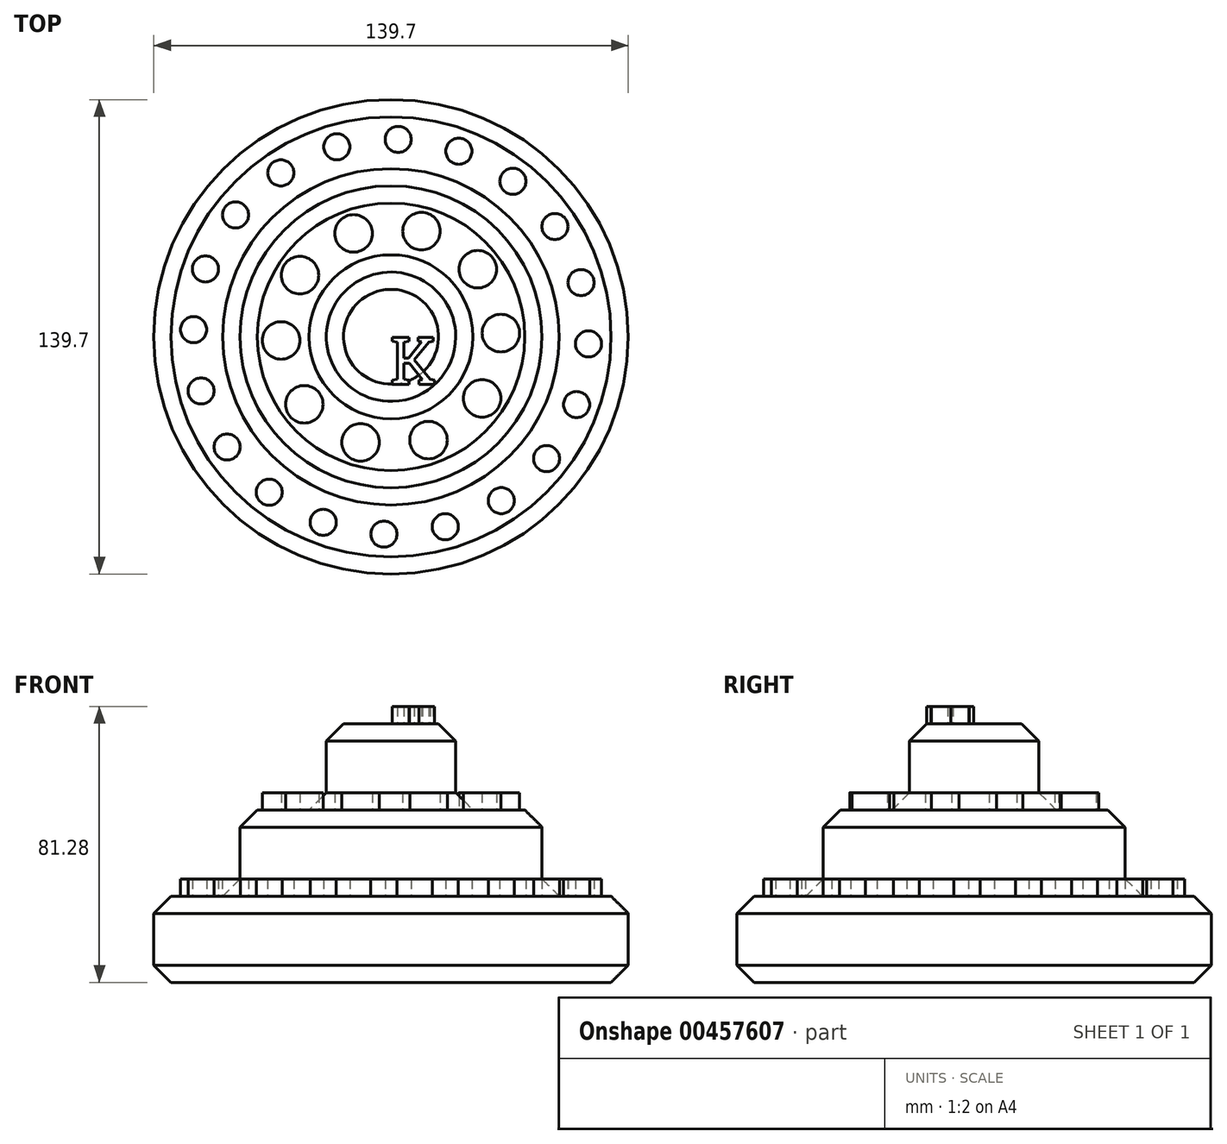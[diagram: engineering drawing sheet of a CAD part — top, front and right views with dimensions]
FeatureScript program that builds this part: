
annotation { "Feature Type Name" : "Feature", "Feature Type Description" : "" }
export const myFeature = defineFeature(function(context is Context, id is Id, definition is map)
    precondition{}
    {
        {
            var Q0;
            Q0=qCreatedBy(makeId("Top.planeOp"),FACE);
            var sketch = newSketch(context, id + "F0", { "sketchPlane" : qUnion([Q0])});
            skCircle(sketch, "E0", {"center": v(0, 0) * mm, "radius": 69.85 * mm});
            skSolve(sketch);
        }
        {
            var Q0;
            Q0=makeQuery(id+"F0.imprint","IMPRINT",FACE,{"disambiguationData":[TD([[makeQuery(id+"F0.imprint","IMPRINT",EDGE,{"derivedFrom":sQuery(id+"F0.wireOp",EDGE,"E0")}),1.0]])]});
            extrude(context, id + "F1", {"entities" : qUnion([Q0]), "depth" : 25.4 * mm});
        }
        {
            var Q0;
            Q0=qCreatedBy(makeId("Top.planeOp"),FACE);
            var sketch = newSketch(context, id + "F2", { "sketchPlane" : qUnion([Q0])});
            skCircle(sketch, "E1", {"center": v(0, 0) * mm, "radius": 44.45 * mm});
            skSolve(sketch);
        }
        {
            var Q0;
            Q0=makeQuery(id+"F2.imprint","IMPRINT",FACE,{"disambiguationData":[TD([[makeQuery(id+"F2.imprint","IMPRINT",EDGE,{"derivedFrom":sQuery(id+"F2.wireOp",EDGE,"E1")}),1.0]])]});
            extrude(context, id + "F3", {"entities" : qUnion([Q0]), "operationType" : NewBodyOperationType.ADD, "depth" : 50.8 * mm});
        }
        {
            var Q0;
            Q0=qCreatedBy(makeId("Top.planeOp"),FACE);
            var sketch = newSketch(context, id + "F4", { "sketchPlane" : qUnion([Q0])});
            skCircle(sketch, "E2", {"center": v(0, 0) * mm, "radius": 19.05 * mm});
            skSolve(sketch);
        }
        {
            var Q0;
            Q0 = qSketchRegion(id + "F4", true);
            extrude(context, id + "F5", {"entities" : qUnion([Q0]), "operationType" : NewBodyOperationType.ADD, "depth" : 76.2 * mm});
        }
        {
            var Q0;
            Q0=makeQuery(id+"F5.opExtrude","CAP_EDGE",EDGE,{"disambiguationData":[OSD([sQuery(id+"F4.wireOp",EDGE,"E2")])],"isStart":false});
            var Q1;
            Q1=makeQuery(id+"F3.opExtrude","CAP_FACE",FACE,{"disambiguationData":[OSD([sQuery(id+"F2.wireOp",EDGE,"E1")])],"isStart":false});
            var Q2;
            Q2=makeQuery(id+"F1.opExtrude","CAP_EDGE",EDGE,{"disambiguationData":[OSD([sQuery(id+"F0.wireOp",EDGE,"E0")])],"isStart":false});
            var Q3;
            Q3=makeQuery(id+"F3.boolean.opBoolean","INTERSECT",EDGE,{"derivedFrom":[makeQuery(id+"F1.opExtrude","CAP_FACE",FACE,{"disambiguationData":[OSD([sQuery(id+"F0.wireOp",EDGE,"E0")])],"isStart":false}),makeQuery(id+"F3.opExtrude","SWEPT_FACE",FACE,{"disambiguationData":[OSD([sQuery(id+"F2.wireOp",EDGE,"E1")])]})]});
            var Q4;
            Q4=makeQuery(id+"F1.opExtrude","CAP_EDGE",EDGE,{"disambiguationData":[OSD([sQuery(id+"F0.wireOp",EDGE,"E0")])],"isStart":true});
            chamfer(context, id + "F6", {"entities" : qUnion([Q0, Q1, Q2, Q3, Q4]), "width" : 5.08 * mm, "tangentPropagation" : true});
        }
        {
            var Q0;
            Q0=makeQuery(id+"F1.opExtrude","CAP_FACE",FACE,{"disambiguationData":[OSD([sQuery(id+"F0.wireOp",EDGE,"E0")])],"isStart":false});
            var sketch = newSketch(context, id + "F7", { "sketchPlane" : qUnion([Q0])});
            skCircle(sketch, "E3", {"center": v(15.96, -55.93) * mm, "radius": 3.84 * mm});
            skSolve(sketch);
        }
        {
            var Q0;
            Q0=makeQuery(id+"F7.imprint","IMPRINT",FACE,{"disambiguationData":[TD([[makeQuery(id+"F7.imprint","IMPRINT",EDGE,{"derivedFrom":sQuery(id+"F7.wireOp",EDGE,"E3")}),1.0]])]});
            var Q1;
            Q1=sQuery(id+"F7.wireOp",EDGE,"E3");
            extrude(context, id + "F8", {"entities" : qUnion([Q0]), "surfaceEntities" : qUnion([Q1]), "depth" : 5.08 * mm});
        }
        {
            var Q0;
            Q0=makeQuery(id+"F8.opExtrude","SWEPT_BODY",BODY,{"disambiguationData":[OSD([sQuery(id+"F7.wireOp",EDGE,"E3")])]});
            var Q1;
            Q1=makeQuery(id+"F6.opChamfer","BLEND_FACE",FACE,{"disambiguationData":[OSD([sQuery(id+"F0.wireOp",EDGE,"E0"),sQuery(id+"F2.wireOp",EDGE,"E1")])]});
            circularPattern(context, id + "F9", {"entities" : qUnion([Q0]), "axis" : qUnion([Q1]), "angle" : 360 * degree, "instanceCount" : 20, "equalSpace" : true});
        }
        {
            var Q0;
            Q0=makeQuery(id+"F3.opExtrude","CAP_FACE",FACE,{"disambiguationData":[OSD([sQuery(id+"F2.wireOp",EDGE,"E1")])],"isStart":false});
            var sketch = newSketch(context, id + "F10", { "sketchPlane" : qUnion([Q0])});
            skSolve(sketch);
        }
        {
            var Q0;
            {var subQ0=sQuery(id+"F2.wireOp",EDGE,"E1");var subQ1=makeQuery(id+"F3.opExtrude","CAP_FACE",FACE,{"disambiguationData":[OSD([subQ0])],"isStart":false});var subQ2=subQ1;Q0=makeQuery(id+"F10.imprint","IMPRINT",FACE,{"disambiguationData":[TD([[makeQuery(id+"F10.imprint","IMPRINT",EDGE,{"derivedFrom":makeQuery(id+"F6.opChamfer","BLEND_EDGE",EDGE,{"blendedFrom":[makeQuery(id+"F3.opExtrude","CAP_EDGE",EDGE,{"disambiguationData":[OSD([subQ0])],"isStart":false}),subQ2],"blendedInto":[subQ2]})}),1.0]])]});}
            var sketch = newSketch(context, id + "F11", { "sketchPlane" : qUnion([Q0])});
            skCircle(sketch, "E4", {"center": v(25.53, 19.9) * mm, "radius": 5.53 * mm});
            skSolve(sketch);
        }
        {
            var Q0;
            Q0=makeQuery(id+"F11.imprint","IMPRINT",FACE,{"disambiguationData":[TD([[makeQuery(id+"F11.imprint","IMPRINT",EDGE,{"derivedFrom":sQuery(id+"F11.wireOp",EDGE,"E4")}),1.0]])]});
            extrude(context, id + "F12", {"entities" : qUnion([Q0]), "depth" : 5.08 * mm});
        }
        {
            var Q0;
            Q0=makeQuery(id+"F12.opExtrude","SWEPT_BODY",BODY,{"disambiguationData":[OSD([sQuery(id+"F11.wireOp",EDGE,"E4")])]});
            var Q1;
            {var subQ0=sQuery(id+"F2.wireOp",EDGE,"E1");Q1=makeQuery(id+"F6.opChamfer","BLEND_EDGE",EDGE,{"blendedFrom":[makeQuery(id+"F3.opExtrude","CAP_EDGE",EDGE,{"disambiguationData":[OSD([subQ0])],"isStart":false}),makeQuery(id+"F3.opExtrude","CAP_FACE",FACE,{"disambiguationData":[OSD([subQ0])],"isStart":false})],"blendedInto":[makeQuery(id+"F3.opExtrude","CAP_FACE",FACE,{"disambiguationData":[OSD([subQ0])],"isStart":false})]});}
            circularPattern(context, id + "F13", {"entities" : qUnion([Q0]), "axis" : qUnion([Q1]), "angle" : 360 * degree, "instanceCount" : 10, "equalSpace" : true});
        }
        {
            var Q0;
            Q0=makeQuery(id+"F5.opExtrude","CAP_FACE",FACE,{"disambiguationData":[OSD([sQuery(id+"F4.wireOp",EDGE,"E2")])],"isStart":false});
            var sketch = newSketch(context, id + "F14", { "sketchPlane" : qUnion([Q0])});
            skText(sketch, "E5", { "text": "K", "fontName": "RobotoSlab-Regular.ttf"});
            const initialGuessF14  = {"E5": [-0.00033, -0.01397, 1, 0, 0.01397]};
            skSetInitialGuess(sketch, initialGuessF14);
            skSolve(sketch);
        }
        {
            var Q0;
            Q0 = qSketchRegion(id + "F14", true);
            extrude(context, id + "F15", {"entities" : qUnion([Q0]), "operationType" : NewBodyOperationType.ADD, "depth" : 5.08 * mm});
        }
    });
